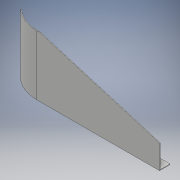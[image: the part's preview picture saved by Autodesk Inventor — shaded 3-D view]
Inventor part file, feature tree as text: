
AUTODESK INVENTOR PART (.ipt)
format: ipt  version: 2018 (Build 220112000, 112)  size: 130,560 bytes
history: native  units: mm
features: other x4, projected_geometry x2, extrude x1, sketch x1
ambient origin geometry x8: Origin, YZ Plane, XZ Plane, XY Plane, X Axis, Y Axis, Z Axis, Center Point
bodies: Body1 (feature_tree)
feature tree (8):
  other  "endplate_ver2.ipt"
  extrude  "押し出し1"  Depth=10.0mm
  other  "ソリッド2::endplate_ver2.ipt"
  other  "TaggingFeature1"
  sketch  "スケッチ1"
  projected_geometry  "投影ループ1"
  projected_geometry  "投影ループ2"
  other  "ソリッド1"
